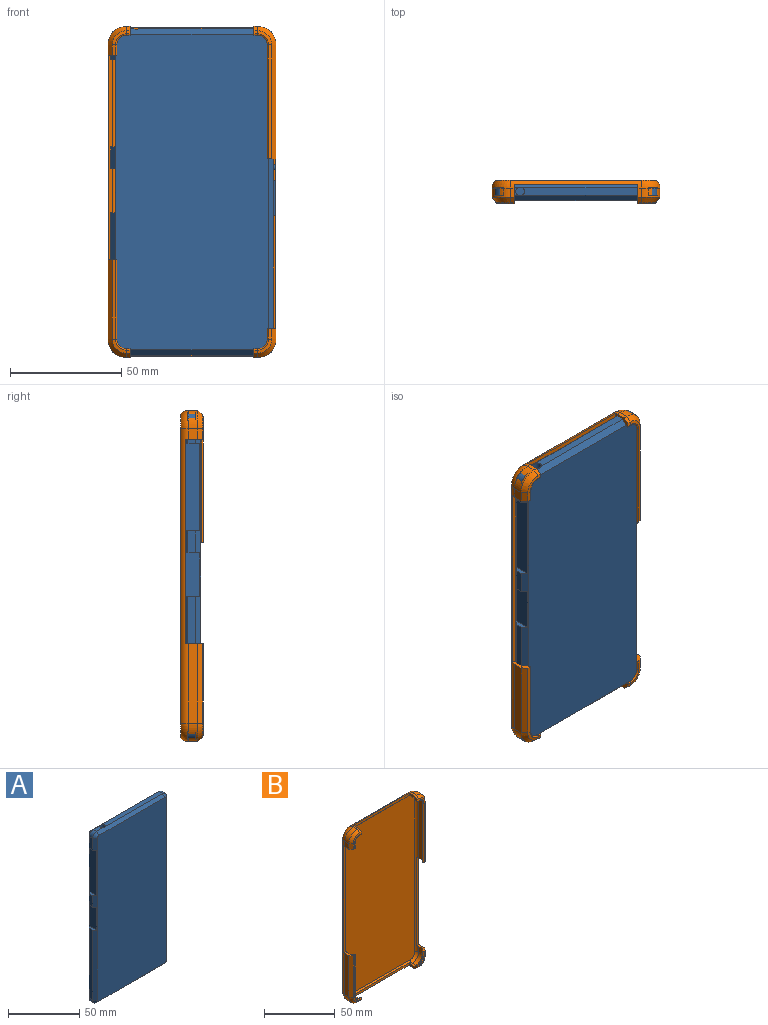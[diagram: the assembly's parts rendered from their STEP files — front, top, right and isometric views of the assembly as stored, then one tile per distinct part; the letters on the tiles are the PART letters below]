
ASSEMBLY  parts=2 mates=1
PART A: 48 faces, bbox 74.2x8x146.8 mm
  f0: plane 93.4x3.4mm, normal (1,0,0), area 289mm2, adj f1,f2,f14,f39,f41,f43,f44,f45
  f1: plane 138.8x2.3mm, normal (0.71,0.71,0), area 369.4mm2, adj f0,f10,f13,f19,f21,f38,f39,f40
  f2: plane 138.8x2.3mm, normal (0.71,-0.71,0), area 369.4mm2, adj f0,f10,f12,f25,f27,f38,f39,f40
  f3: plane 6.45x3.4mm, normal (0,0,1), area 19.6mm2, adj f16,f18,f24,f36
  f4: plane 56.65x3.4mm, normal (0,0,1), area 190.3mm2, adj f15,f18,f24,f36
  f5: plane 9.9x3.4mm, normal (-1,0,0), area 33.7mm2, adj f7,f8,f16,f33
  f6: plane 9.9x3.4mm, normal (-1,0,0), area 33.7mm2, adj f7,f8,f30,f34
  f7: plane 138.8x2.3mm, normal (-0.71,0.71,0), area 284.9mm2, adj f5,f6,f11,f13,f20,f22,f30,f31
  f8: plane 138.8x2.3mm, normal (-0.71,-0.71,0), area 284.9mm2, adj f5,f6,f11,f12,f26,f28,f30,f31
  f9: plane 65.2x3.4mm, normal (0,0,-1), area 221.7mm2, adj f14,f17,f23,f29
  f10: plane 16.4x3.4mm, normal (1,0,0), area 55.8mm2, adj f1,f2,f15,f38
  f11: plane 60.1x3.4mm, normal (-1,0,0), area 204.3mm2, adj f7,f8,f17,f31
  f12: plane 142.2x68.6mm, normal (0,-1,0), area 9752.4mm2, adj f2,f8,f24,f25,f26,f27,f28,f29
  f13: plane 142.2x68.6mm, normal (0,1,0), area 9752.4mm2, adj f1,f7,f18,f19,f20,f21,f22,f23
  f14: cylinder r=4mm len=4mm, axis (0,-1,0), area 21.4mm2, adj f0,f9,f21,f27
  f15: cylinder r=4mm len=4mm, axis (0,1,0), area 21.4mm2, adj f4,f10,f19,f25
  f16: cylinder r=4mm len=4mm, axis (0,-1,0), area 21.4mm2, adj f3,f5,f20,f26
  f17: cylinder r=4mm len=4mm, axis (0,1,0), area 21.4mm2, adj f9,f11,f22,f28
  f18: plane 65.2x2.3mm, normal (0,0.71,0.71), area 211.5mm2, adj f3,f4,f13,f19,f20,f36
  f19: cone r=1.7mm half-angle=45deg, axis (0,-1,0), area 14.6mm2, adj f1,f13,f15,f18
  f20: cone r=1.7mm half-angle=45deg, axis (0,-1,0), area 14.6mm2, adj f7,f13,f16,f18
  f21: cone r=1.7mm half-angle=45deg, axis (0,-1,0), area 14.6mm2, adj f1,f13,f14,f23
  f22: cone r=1.7mm half-angle=45deg, axis (0,-1,0), area 14.6mm2, adj f7,f13,f17,f23
  f23: plane 65.2x2.3mm, normal (0,0.71,-0.71), area 212.1mm2, adj f9,f13,f21,f22
  f24: plane 65.2x2.3mm, normal (0,-0.71,0.71), area 211.5mm2, adj f3,f4,f12,f25,f26,f36
  f25: cone r=1.7mm half-angle=45deg, axis (0,1,0), area 14.6mm2, adj f2,f12,f15,f24
  f26: cone r=1.7mm half-angle=45deg, axis (0,1,0), area 14.6mm2, adj f8,f12,f16,f24
  f27: cone r=1.7mm half-angle=45deg, axis (0,1,0), area 14.6mm2, adj f2,f12,f14,f29
  f28: cone r=1.7mm half-angle=45deg, axis (0,1,0), area 14.6mm2, adj f8,f12,f17,f29
  f29: plane 65.2x2.3mm, normal (0,-0.71,-0.71), area 212.1mm2, adj f9,f12,f27,f28
  f30: plane 7.4x2mm, normal (0,0,-1), area 10.8mm2, adj f6,f7,f8,f32
  f31: plane 7.4x2mm, normal (0,0,1), area 10.8mm2, adj f7,f8,f11,f32
  f32: plane 19.7x7.4mm, normal (-1,0,0), area 145.8mm2, adj f7,f8,f30,f31
  f33: plane 7.4x2mm, normal (0,0,-1), area 10.8mm2, adj f5,f7,f8,f35
  f34: plane 7.4x2mm, normal (0,0,1), area 10.8mm2, adj f6,f7,f8,f35
  f35: plane 39.2x7.4mm, normal (-1,0,0), area 290.1mm2, adj f7,f8,f33,f34
  f36: cylinder r=2mm len=5mm, axis (0,0,1), area 61.9mm2, adj f3,f4,f18,f24,f37
  f37: plane 4x4mm, normal (0,0,1), area 12.6mm2, adj f36
  f38: plane 7.4x2mm, normal (0,0,-1), area 10.8mm2, adj f1,f2,f10,f40
  f39: plane 7.4x2mm, normal (0,0,1), area 10.8mm2, adj f0,f1,f2,f40
  f40: plane 29x7.4mm, normal (1,0,0), area 214.6mm2, adj f1,f2,f38,f39
  f41: cylinder r=1.25mm len=2.5mm, axis (-1,0,0), area 7.9mm2, adj f0,f42
  f42: plane 2.5x2.5mm, normal (1,0,0), area 4.9mm2, adj f41
  f43: plane 15.8x1mm, normal (0,-1,0), area 15.8mm2, adj f0,f44,f46,f47
  f44: plane 1.5x1mm, normal (0,0,-1), area 1.5mm2, adj f0,f43,f45,f47
  f45: plane 15.8x1mm, normal (0,1,0), area 15.8mm2, adj f0,f44,f46,f47
  f46: plane 1.5x1mm, normal (0,0,1), area 1.5mm2, adj f0,f43,f45,f47
  f47: plane 15.8x1.5mm, normal (1,0,0), area 23.7mm2, adj f43,f44,f45,f46
PART B: 102 faces, bbox 75.6x10.2x149 mm
  f0: plane 4.16x1.7mm, normal (0,0,-1), area 7.1mm2, adj f5,f40,f47,f101
  f1: plane 3.5x1.7mm, normal (0,0,1), area 5.9mm2, adj f2,f33,f42,f101
  f2: plane 2.4x2.01mm, normal (0,0.64,0.77), area 5.3mm2, adj f1,f3,f43,f101
  f3: cylinder r=0.5mm len=1.7mm, axis (-1,0,0), area 2.1mm2, adj f2,f4,f44,f101
  f4: plane 1.7x1.38mm, normal (0,-0.98,-0.17), area 2.4mm2, adj f3,f5,f45,f101
  f5: plane 2.31x1.94mm, normal (0,-0.64,-0.77), area 5.1mm2, adj f0,f4,f46,f101
  f6: plane 3.5x1.7mm, normal (0,0,-1), area 5.9mm2, adj f7,f58,f65,f96
  f7: plane 2.4x2.01mm, normal (0,0.64,-0.77), area 5.3mm2, adj f6,f8,f59,f96
  f8: cylinder r=0.5mm len=1.7mm, axis (1,0,0), area 2.1mm2, adj f7,f9,f60,f96
  f9: plane 1.7x1.38mm, normal (0,-0.98,0.17), area 2.4mm2, adj f8,f10,f61,f96
  f10: plane 2.31x1.94mm, normal (0,-0.64,0.77), area 5.1mm2, adj f9,f11,f62,f96
  f11: plane 4.16x1.7mm, normal (0,0,1), area 7.1mm2, adj f10,f63,f72,f96
  f12: plane 4.7x1.38mm, normal (0.17,-0.98,0), area 6.6mm2, adj f13,f17,f45,f94
  f13: plane 4.7x2.31mm, normal (0.77,-0.64,0), area 14.2mm2, adj f12,f46,f55,f94
  f14: plane 51.2x4.16mm, normal (1,0,0), area 212.7mm2, adj f54,f56,f63,f95
  f15: plane 51.2x3.5mm, normal (-1,0,0), area 179.2mm2, adj f16,f49,f58,f95
  f16: plane 51.2x2.4mm, normal (-0.77,0.64,0), area 160.4mm2, adj f15,f52,f59,f95
  f17: cylinder r=0.5mm len=4.7mm, axis (0,0,-1), area 5.9mm2, adj f12,f44,f51,f94
  f18: plane 35.7x1.38mm, normal (-0.17,-0.98,0), area 50mm2, adj f19,f23,f29,f92
  f19: plane 35.7x2.31mm, normal (-0.77,-0.64,0), area 107.7mm2, adj f18,f30,f87,f92
  f20: plane 4.7x4.16mm, normal (-1,0,0), area 19.5mm2, adj f24,f79,f86,f91
  f21: plane 4.7x3.5mm, normal (1,0,0), area 16.4mm2, adj f22,f74,f81,f91
  f22: plane 4.7x2.4mm, normal (0.77,0.64,0), area 14.7mm2, adj f21,f75,f84,f91
  f23: cylinder r=0.5mm len=35.7mm, axis (0,0,1), area 44.6mm2, adj f18,f28,f83,f92
  f24: cylinder r=4.63mm len=132.4mm, axis (0,0,1), area 384.7mm2, adj f20,f32,f80,f87,f89,f90,f91,f92
  f25: torus R=3.67mm, axis (0,1,0), area 28.8mm2, adj f26,f33,f81,f88
  f26: cylinder r=6.5mm len=6.5mm, axis (0,1,0), area 35.7mm2, adj f25,f27,f34,f82
  f27: cone r=4.49mm half-angle=40deg, axis (0,1,0), area 27mm2, adj f26,f28,f35,f83
  f28: torus R=4.87mm, axis (0,1,0), area 8.9mm2, adj f23,f27,f29,f36
  f29: cone r=6.36mm half-angle=80deg, axis (0,1,0), area 12.5mm2, adj f18,f28,f30,f37
  f30: cone r=8.3mm half-angle=40deg, axis (0,1,0), area 34.7mm2, adj f19,f29,f31,f38
  f31: cylinder r=8.3mm len=8.3mm, axis (0,1,0), area 54.2mm2, adj f30,f32,f39,f87
  f32: torus R=3.67mm, axis (0,1,0), area 48.3mm2, adj f24,f31,f40,f89
  f33: cylinder r=2.83mm len=59mm, axis (-1,0,0), area 92.8mm2, adj f1,f25,f34,f41,f88,f99,f100,f101
  f34: plane 3.5x1.7mm, normal (0,0,1), area 5.9mm2, adj f26,f33,f35,f99
  f35: plane 2.4x2.01mm, normal (0,0.64,0.77), area 5.3mm2, adj f27,f34,f36,f99
  f36: cylinder r=0.5mm len=1.7mm, axis (-1,0,0), area 2.1mm2, adj f28,f35,f37,f99
  f37: plane 1.7x1.38mm, normal (0,-0.98,-0.17), area 2.4mm2, adj f29,f36,f38,f99
  f38: plane 2.31x1.94mm, normal (0,-0.64,-0.77), area 5.1mm2, adj f30,f37,f39,f99
  f39: plane 4.16x1.7mm, normal (0,0,-1), area 7.1mm2, adj f31,f38,f40,f99
  f40: cylinder r=4.63mm len=59mm, axis (-1,0,0), area 149.1mm2, adj f0,f32,f39,f48,f89,f99,f100,f101
  f41: torus R=3.67mm, axis (0,1,0), area 28.8mm2, adj f33,f42,f49,f88
  f42: cylinder r=6.5mm len=6.5mm, axis (0,1,0), area 35.7mm2, adj f1,f41,f43,f50
  f43: cone r=4.49mm half-angle=40deg, axis (0,1,0), area 27mm2, adj f2,f42,f44,f51
  f44: torus R=4.87mm, axis (0,1,0), area 8.9mm2, adj f3,f17,f43,f45
  f45: cone r=6.36mm half-angle=80deg, axis (0,1,0), area 12.5mm2, adj f4,f12,f44,f46
  f46: cone r=8.3mm half-angle=40deg, axis (0,1,0), area 34.7mm2, adj f5,f13,f45,f47
  f47: cylinder r=8.3mm len=8.3mm, axis (0,1,0), area 54.2mm2, adj f0,f46,f48,f55
  f48: torus R=3.67mm, axis (0,1,0), area 48.3mm2, adj f40,f47,f56,f89
  f49: cylinder r=2.83mm len=132.4mm, axis (0,0,-1), area 284.5mm2, adj f15,f41,f50,f57,f88,f93,f94,f95
  f50: plane 4.7x3.5mm, normal (-1,0,0), area 16.5mm2, adj f42,f49,f51,f94
  f51: plane 4.7x2.4mm, normal (-0.77,0.64,0), area 14.7mm2, adj f17,f43,f50,f94
  f52: cylinder r=0.5mm len=51.2mm, axis (0,0,-1), area 64mm2, adj f16,f53,f60,f95
  f53: plane 51.2x1.38mm, normal (0.17,-0.98,0), area 71.7mm2, adj f52,f54,f61,f95
  f54: plane 51.2x2.31mm, normal (0.77,-0.64,0), area 154.4mm2, adj f14,f53,f62,f95
  f55: plane 4.7x4.16mm, normal (1,0,0), area 19.5mm2, adj f13,f47,f56,f94
  f56: cylinder r=4.63mm len=132.4mm, axis (0,0,-1), area 408.4mm2, adj f14,f48,f55,f64,f89,f93,f94,f95
  f57: torus R=3.67mm, axis (0,1,0), area 28.8mm2, adj f49,f58,f65,f88
  f58: cylinder r=6.5mm len=6.5mm, axis (0,1,0), area 35.7mm2, adj f6,f15,f57,f59
  f59: cone r=4.49mm half-angle=40deg, axis (0,1,0), area 27mm2, adj f7,f16,f58,f60
  f60: torus R=4.87mm, axis (0,1,0), area 8.9mm2, adj f8,f52,f59,f61
  f61: cone r=6.36mm half-angle=80deg, axis (0,1,0), area 12.5mm2, adj f9,f53,f60,f62
  f62: cone r=8.3mm half-angle=40deg, axis (0,1,0), area 34.7mm2, adj f10,f54,f61,f63
  f63: cylinder r=8.3mm len=8.3mm, axis (0,1,0), area 54.2mm2, adj f11,f14,f62,f64
  f64: torus R=3.67mm, axis (0,1,0), area 48.3mm2, adj f56,f63,f72,f89
  f65: cylinder r=2.83mm len=59mm, axis (1,0,0), area 92.8mm2, adj f6,f57,f66,f73,f88,f96,f97,f98
  f66: plane 3.5x1.7mm, normal (0,0,-1), area 5.9mm2, adj f65,f67,f74,f98
  f67: plane 2.4x2.01mm, normal (0,0.64,-0.77), area 5.3mm2, adj f66,f68,f75,f98
  f68: cylinder r=0.5mm len=1.7mm, axis (1,0,0), area 2.1mm2, adj f67,f69,f76,f98
  f69: plane 1.7x1.38mm, normal (0,-0.98,0.17), area 2.4mm2, adj f68,f70,f77,f98
  f70: plane 2.31x1.94mm, normal (0,-0.64,0.77), area 5.1mm2, adj f69,f71,f78,f98
  f71: plane 4.16x1.7mm, normal (0,0,1), area 7.1mm2, adj f70,f72,f79,f98
  f72: cylinder r=4.63mm len=59mm, axis (1,0,0), area 149.1mm2, adj f11,f64,f71,f80,f89,f96,f97,f98
  f73: torus R=3.67mm, axis (0,1,0), area 28.8mm2, adj f65,f74,f81,f88
  f74: cylinder r=6.5mm len=6.5mm, axis (0,1,0), area 35.7mm2, adj f21,f66,f73,f75
  f75: cone r=4.49mm half-angle=40deg, axis (0,1,0), area 27mm2, adj f22,f67,f74,f76
  f76: torus R=4.87mm, axis (0,1,0), area 8.9mm2, adj f68,f75,f77,f84
  f77: cone r=6.36mm half-angle=80deg, axis (0,1,0), area 12.5mm2, adj f69,f76,f78,f85
  f78: cone r=8.3mm half-angle=40deg, axis (0,1,0), area 34.7mm2, adj f70,f77,f79,f86
  f79: cylinder r=8.3mm len=8.3mm, axis (0,1,0), area 54.2mm2, adj f20,f71,f78,f80
  f80: torus R=3.67mm, axis (0,1,0), area 48.3mm2, adj f24,f72,f79,f89
  f81: cylinder r=2.83mm len=132.4mm, axis (0,0,1), area 260mm2, adj f21,f25,f73,f82,f88,f90,f91,f92
  f82: plane 35.7x3.5mm, normal (1,0,0), area 124.9mm2, adj f26,f81,f83,f92
  f83: plane 35.7x2.4mm, normal (0.77,0.64,0), area 111.8mm2, adj f23,f27,f82,f92
  f84: cylinder r=0.5mm len=4.7mm, axis (0,0,1), area 5.9mm2, adj f22,f76,f85,f91
  f85: plane 4.7x1.38mm, normal (-0.17,-0.98,0), area 6.6mm2, adj f77,f84,f86,f91
  f86: plane 4.7x2.31mm, normal (-0.77,-0.64,0), area 14.2mm2, adj f20,f78,f85,f91
  f87: plane 35.7x4.16mm, normal (-1,0,0), area 148.3mm2, adj f19,f24,f31,f92
  f88: plane 142.4x69mm, normal (0,-1,0), area 9804.1mm2, adj f25,f33,f41,f49,f57,f65,f73,f81
  f89: plane 145.81x72.41mm, normal (0,1,0), area 10518.6mm2, adj f24,f32,f40,f48,f56,f64,f72,f80
  f90: plane 92x1.98mm, normal (0,-1,0), area 182.2mm2, adj f24,f81,f91,f92
  f91: plane 8.22x3.93mm, normal (0,0,-1), area 16.1mm2, adj f20,f21,f22,f24,f81,f84,f85,f86
  f92: plane 8.22x3.93mm, normal (0,0,1), area 16.1mm2, adj f18,f19,f23,f24,f81,f82,f83,f87
  f93: plane 76.5x1.98mm, normal (0,-1,0), area 151.5mm2, adj f49,f56,f94,f95
  f94: plane 8.22x3.93mm, normal (0,0,1), area 16.1mm2, adj f12,f13,f17,f49,f50,f51,f55,f56
  f95: plane 8.22x3.93mm, normal (0,0,-1), area 16.1mm2, adj f14,f15,f16,f49,f52,f53,f54,f56
  f96: plane 8.22x3.93mm, normal (-1,0,0), area 16.1mm2, adj f6,f7,f8,f9,f10,f11,f65,f72
  f97: plane 55.6x1.98mm, normal (0,-1,0), area 110.1mm2, adj f65,f72,f96,f98
  f98: plane 8.22x3.93mm, normal (1,0,0), area 16.1mm2, adj f65,f66,f67,f68,f69,f70,f71,f72
  f99: plane 8.22x3.93mm, normal (1,0,0), area 16.1mm2, adj f33,f34,f35,f36,f37,f38,f39,f40
  f100: plane 55.6x1.98mm, normal (0,-1,0), area 110.1mm2, adj f33,f40,f99,f101
  f101: plane 8.22x3.93mm, normal (-1,0,0), area 16.1mm2, adj f0,f1,f2,f3,f4,f5,f33,f40
PLACE A t=(9.11,60.42,12.14)mm
PLACE B t=(9.11,64.92,12.14)mm
MATE fastened A.f13 <-> B.f88  axis (0,1,0) through (9.11,64.42,12.14)mm
